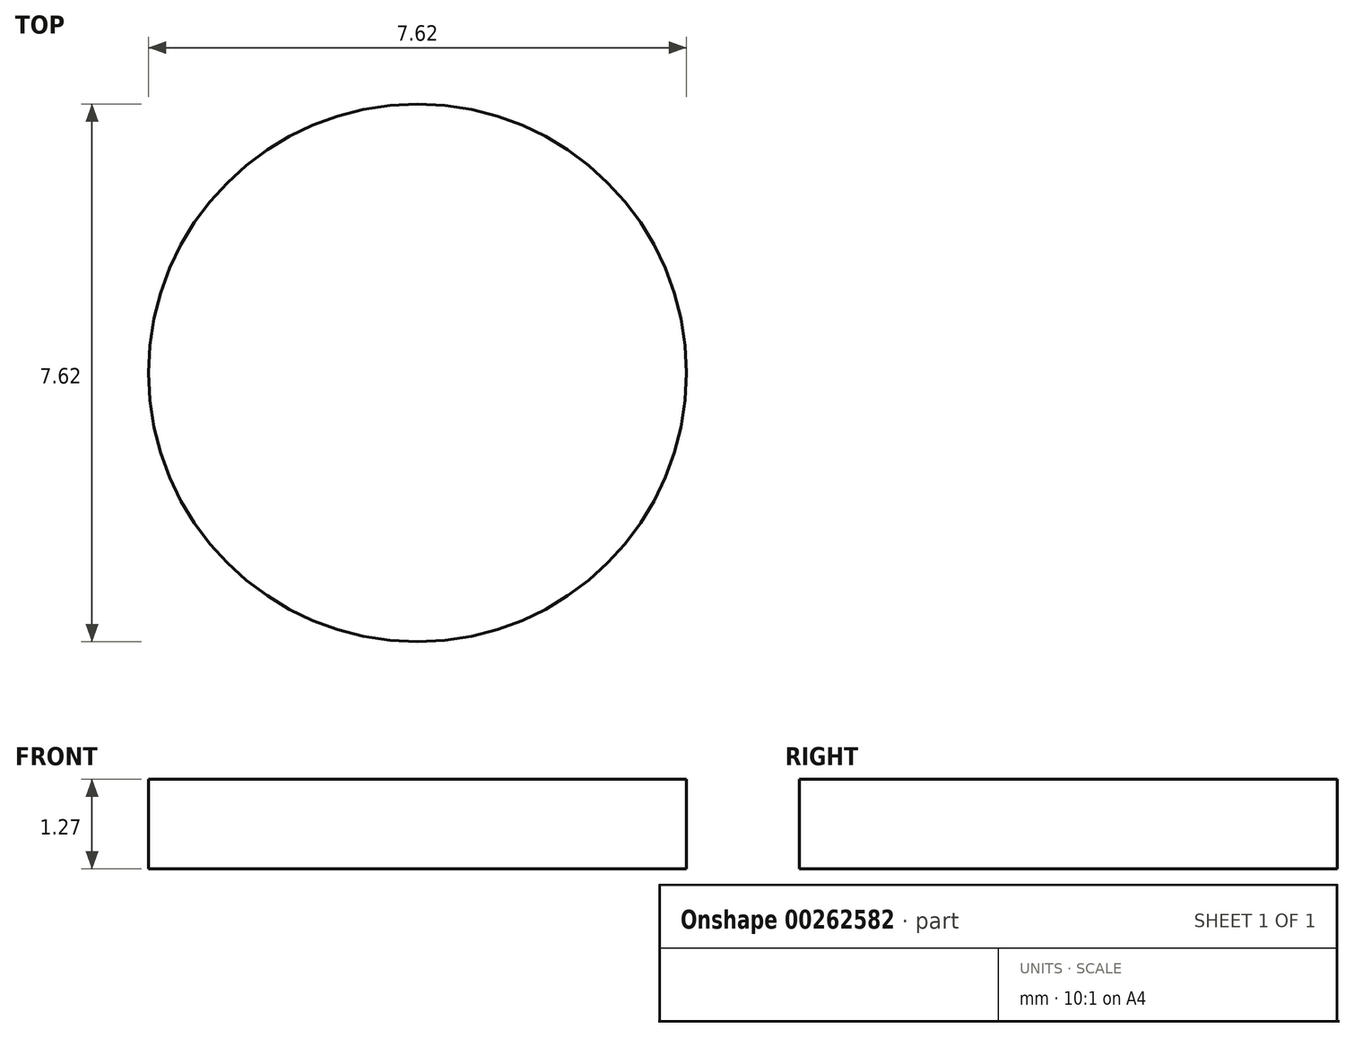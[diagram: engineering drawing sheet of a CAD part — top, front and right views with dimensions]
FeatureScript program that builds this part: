
annotation { "Feature Type Name" : "Feature", "Feature Type Description" : "" }
export const myFeature = defineFeature(function(context is Context, id is Id, definition is map)
    precondition{}
    {
        {
            var Q0;
            Q0=qCreatedBy(makeId("Top.planeOp"),FACE);
            var sketch = newSketch(context, id + "F0", { "sketchPlane" : qUnion([Q0])});
            skCircle(sketch, "E0", {"center": v(0, 0) * mm, "radius": 3.81 * mm});
            skSolve(sketch);
        }
        {
            var Q0;
            Q0 = qSketchRegion(id + "F0", true);
            extrude(context, id + "F1", {"entities" : qUnion([Q0]), "depth" : 1.27 * mm});
        }
    });
